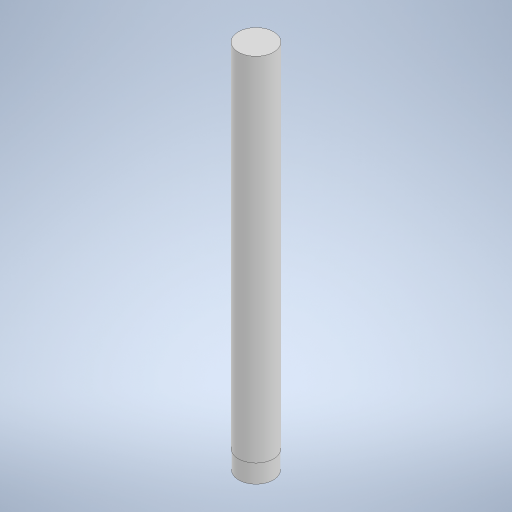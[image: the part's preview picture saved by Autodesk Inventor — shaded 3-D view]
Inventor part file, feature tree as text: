
AUTODESK INVENTOR PART (.ipt)
format: ipt  version: 2024 (Build 280153000, 153)  size: 230,400 bytes
history: native  units: mm
features: extrude x2, sketch x2
ambient origin geometry x8: Origin, YZ Plane, XZ Plane, XY Plane, X Axis, Y Axis, Z Axis, Center Point
bodies: Solide1 (feature_tree)
feature tree (4):
  extrude  "Extrusion1"  Depth=15.0mm
  extrude  "Extrusion2"  Depth=150.0mm TaperAngle=0.0deg
  sketch  "Esquisse1"
  sketch  "Esquisse2"
